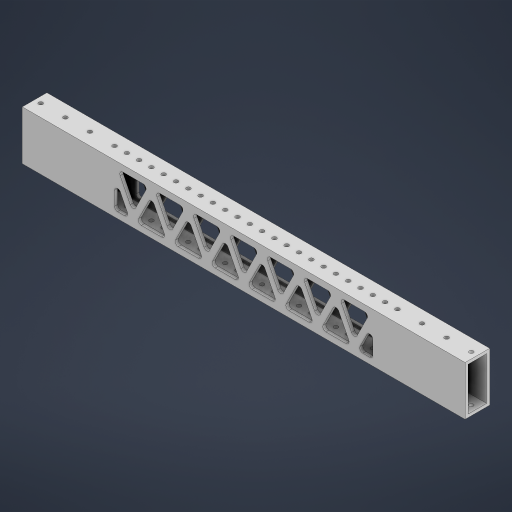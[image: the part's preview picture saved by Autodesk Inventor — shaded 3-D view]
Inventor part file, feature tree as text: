
AUTODESK INVENTOR PART (.ipt)
format: ipt  version: 2023 (Build 270158000, 158)  size: 530,432 bytes
history: native  units: in
note: dims shown in document units (in); Inventor stores cm internally (conversion verified against a paired STEP export)
features: sketch x5, extrude x3, hole x2, pattern_linear x2, plane x2, mirror x2, fillet x2, shell x1
ambient origin geometry x8: Origin, YZ Plane, XZ Plane, XY Plane, X Axis, Y Axis, Z Axis, Center Point
bodies: Solid1 (feature_tree)
feature tree (19):
  extrude  "Extrusion1"  Depth=1.0in
  shell  "Shell1"  Thickness=18.0in
  hole  "Hole1"  [1 undecoded]
  pattern_linear  "Rectangular Pattern1"  Count1=4 Spacing1=1.0in
  plane  "Work Plane1"
  mirror  "Mirror1"
  hole  "Hole2"  [1 undecoded]
  pattern_linear  "Rectangular Pattern2"  Spacing1=0.1625in  [1 undecoded]
  extrude  "Extrusion2"  Depth=0.125in
  extrude  "Extrusion5"  Depth=0.125in
  fillet  "Fillet4"  Radius=0.125in
  fillet  "Fillet6"  Radius=3.75in
  plane  "Work Plane2"
  mirror  "Mirror2"
  sketch  "Sketch1"  dims[d0=2.0in d1=1.0in d2=18.0in d3=0.0in]
  sketch  "Sketch2"  dims[d5=0.1625in d6=0.25in]
  sketch  "Sketch3"  dims[d7=90.0deg]
  sketch  "Sketch4"  dims[d8=18.0in]
  sketch  "Sketch7"  dims[d9=0.1625in d10=0.75in d11=0.375in d12=0.25in d13=0.5635in d14=1.0in d15=0.8108in d16=1.5748in d18=1.0in d19=-9.0in d20=0.1625in d21=0.5in d22=0.1625in d23=0.75in d24=0.375in d25=0.25in d26=0.5635in d27=1.0in d28=0.8108in d29=8.6614in d31=0.5in d32=0.125in d33=3.75in d34=3.75in d35=0.25in d36=0.25in d37=1.0in d38=0.0in d58=1.5in d59=0.25in d60=0.25in d61=1.0in d62=0.0in d63=0.125in d64=2.7559in d66=1.5in d67=0.3937in d69=1.0in d72=0.125in d73=-0.5in]
note: 3 required parameter values undecoded (feature->parameter linkage not recoverable at this tier; creation-order binding heuristic only, values carry confidence <= 0.55)
